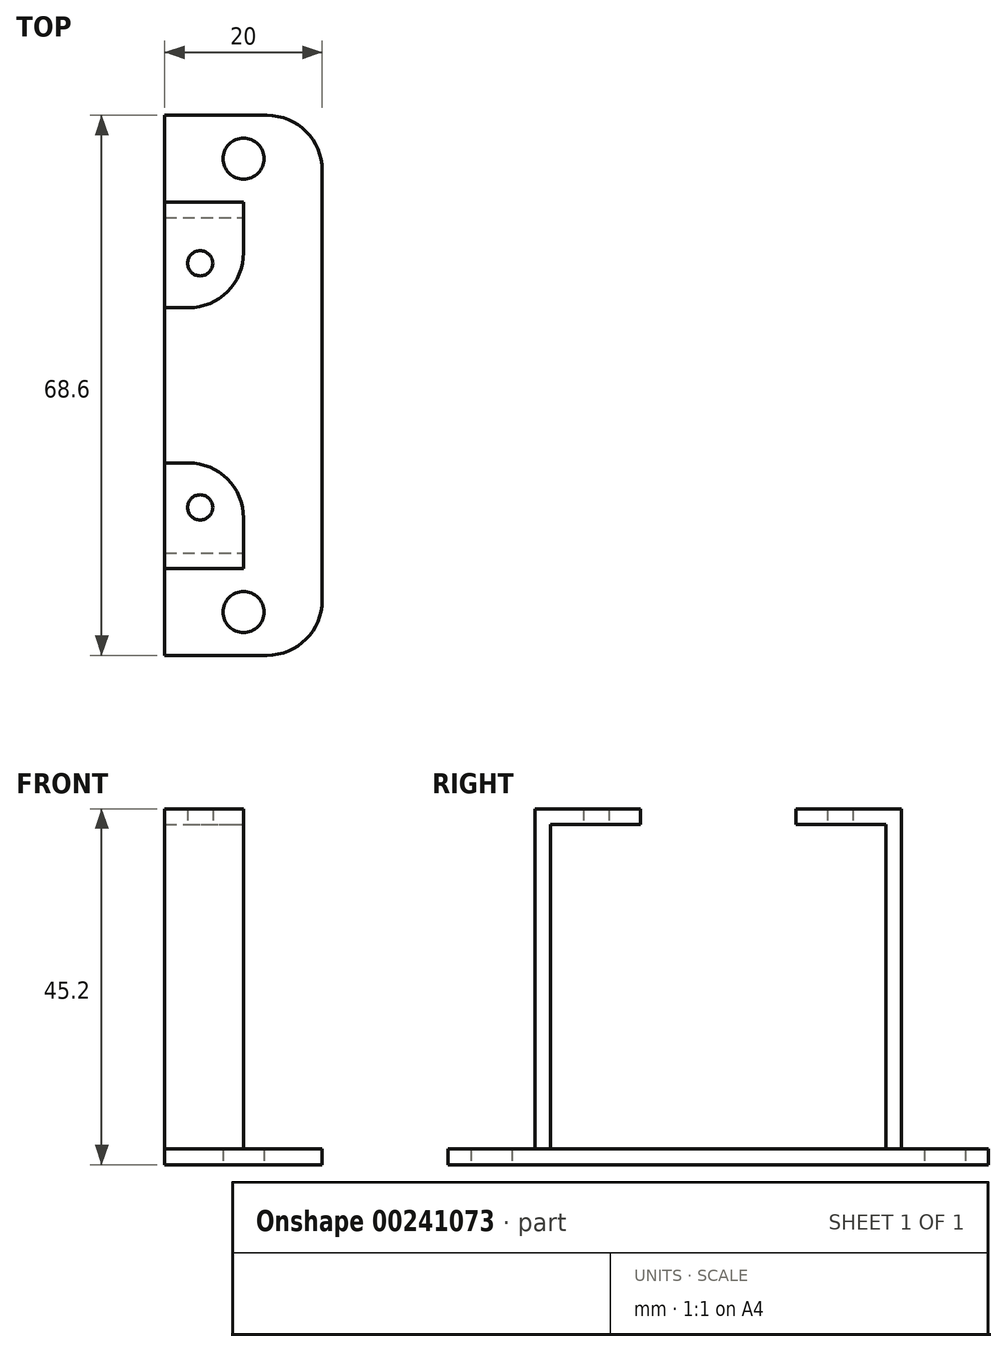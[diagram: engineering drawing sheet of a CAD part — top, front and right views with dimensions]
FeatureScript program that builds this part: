
annotation { "Feature Type Name" : "Feature", "Feature Type Description" : "" }
export const myFeature = defineFeature(function(context is Context, id is Id, definition is map)
    precondition{}
    {
        {
            var Q0;
            Q0=qCreatedBy(makeId("Top.planeOp"),FACE);
            var sketch = newSketch(context, id + "F0", { "sketchPlane" : qUnion([Q0])});
            skLineSegment(sketch, "E0", {"start": v(-61.56, 1.08) * mm, "end": v(-30.56, 1.08) * mm, "construction": true});
            skLineSegment(sketch, "E1", {"start": v(-30.56, 1.08) * mm, "end": v(-30.56, -29.92) * mm, "construction": true});
            skLineSegment(sketch, "E2", {"start": v(-30.56, -29.92) * mm, "end": v(-61.56, -29.92) * mm, "construction": true});
            skLineSegment(sketch, "E3", {"start": v(-61.56, -29.92) * mm, "end": v(-61.56, 1.08) * mm, "construction": true});
            skLineSegment(sketch, "E4", {"start": v(-36.06, 55.81) * mm, "end": v(-36.06, -69.61) * mm, "construction": true});
            skLineSegment(sketch, "E5", {"start": v(-16.06, 55.81) * mm, "end": v(-16.06, -69.61) * mm, "construction": true});
            skLineSegment(sketch, "E6", {"start": v(-6.06, 55.81) * mm, "end": v(-6.06, -69.61) * mm, "construction": true});
            skLineSegment(sketch, "E7.MirrorCS", {"start": v(-56.06, 55.81) * mm, "end": v(-56.06, -69.61) * mm, "construction": true});
            skLineSegment(sketch, "E8.MirrorCS", {"start": v(-66.06, 55.81) * mm, "end": v(-66.06, -69.61) * mm, "construction": true});
            skLineSegment(sketch, "E9.bottom", {"start": v(-67.36, 6.88) * mm, "end": v(-24.76, 6.88) * mm, "construction": true});
            skLineSegment(sketch, "E9.top", {"start": v(-67.36, -35.72) * mm, "end": v(-24.76, -35.72) * mm, "construction": true});
            skLineSegment(sketch, "E9.left", {"start": v(-67.36, 6.88) * mm, "end": v(-67.36, -35.72) * mm, "construction": true});
            skLineSegment(sketch, "E9.right", {"start": v(-24.76, 6.88) * mm, "end": v(-24.76, -35.72) * mm, "construction": true});
            skPoint(sketch, "E10", {"position": v(-24.76, -14.42) * mm});
            skPoint(sketch, "E11", {"position": v(-30.56, -14.42) * mm});
            skPoint(sketch, "E12", {"position": v(-46.06, 1.08) * mm});
            skPoint(sketch, "E13", {"position": v(-46.06, 6.88) * mm});
            skLineSegment(sketch, "E14", {"start": v(-56.06, 55.81) * mm, "end": v(-36.06, 55.81) * mm, "construction": true});
            skPoint(sketch, "E15", {"position": v(-46.06, 55.81) * mm});
            skLineSegment(sketch, "E16", {"start": v(-61.06, 8.88) * mm, "end": v(-61.06, 19.88) * mm, "construction": true});
            skLineSegment(sketch, "E17", {"start": v(-61.06, 19.88) * mm, "end": v(-51.06, 19.88) * mm});
            skLineSegment(sketch, "E18", {"start": v(-51.06, 19.88) * mm, "end": v(-51.06, 8.88) * mm});
            skPoint(sketch, "E19", {"position": v(-56.06, 19.88) * mm});
            skLineSegment(sketch, "E20.bottom", {"start": v(-66.06, 6.88) * mm, "end": v(-56.06, 6.88) * mm});
            skLineSegment(sketch, "E20.top", {"start": v(-66.06, 8.88) * mm, "end": v(-51.06, 8.88) * mm});
            skLineSegment(sketch, "E20.left", {"start": v(-66.06, 6.88) * mm, "end": v(-66.06, 8.88) * mm});
            skLineSegment(sketch, "E21", {"start": v(-95.64, -14.42) * mm, "end": v(16.88, -14.42) * mm, "construction": true});
            skLineSegment(sketch, "E22.MirrorCS", {"start": v(-66.06, -35.72) * mm, "end": v(-51.06, -35.72) * mm});
            skLineSegment(sketch, "E23", {"start": v(-66.06, 6.88) * mm, "end": v(-66.06, -35.72) * mm});
            skLineSegment(sketch, "E24", {"start": v(-56.06, 6.88) * mm, "end": v(-56.06, -35.72) * mm});
            skLineSegment(sketch, "E25", {"start": v(-56.06, 6.88) * mm, "end": v(-56.06, 8.88) * mm});
            skPoint(sketch, "E26.orphan", {"position": v(-51.06, 6.88) * mm});
            skLineSegment(sketch, "E27", {"start": v(-66.06, 8.88) * mm, "end": v(-66.06, 19.88) * mm});
            skLineSegment(sketch, "E28", {"start": v(-66.06, 19.88) * mm, "end": v(-61.06, 19.88) * mm});
            skPoint(sketch, "E29", {"position": v(-56.06, 14.38) * mm});
            skPoint(sketch, "E29.positionSnap0", {"position": v(-51.06, 14.38) * mm});
            skPoint(sketch, "E30", {"position": v(-46.06, -14.42) * mm});
            skLineSegment(sketch, "E31.MirrorCS", {"start": v(-61.06, -48.72) * mm, "end": v(-51.06, -48.72) * mm});
            skLineSegment(sketch, "E32.MirrorCS", {"start": v(-66.06, -48.72) * mm, "end": v(-61.06, -48.72) * mm});
            skLineSegment(sketch, "E33.MirrorCS", {"start": v(-66.06, -37.72) * mm, "end": v(-66.06, -48.72) * mm});
            skLineSegment(sketch, "E34.MirrorCS", {"start": v(-51.06, -48.72) * mm, "end": v(-51.06, -37.72) * mm});
            skLineSegment(sketch, "E35.MirrorCS", {"start": v(-66.06, -37.72) * mm, "end": v(-51.06, -37.72) * mm});
            skLineSegment(sketch, "E36.MirrorCS", {"start": v(-56.06, -35.72) * mm, "end": v(-56.06, -37.72) * mm});
            skLineSegment(sketch, "E37.MirrorCS", {"start": v(-66.06, -35.72) * mm, "end": v(-66.06, -37.72) * mm});
            skPoint(sketch, "E38.MirrorP", {"position": v(-56.06, -43.22) * mm});
            skLineSegment(sketch, "E39", {"start": v(-51.06, 19.88) * mm, "end": v(-46.06, 19.88) * mm});
            skLineSegment(sketch, "E40", {"start": v(-51.06, -48.72) * mm, "end": v(-46.06, -48.72) * mm});
            skPoint(sketch, "E40.endSnap0", {"position": v(-46.06, -35.72) * mm});
            skLineSegment(sketch, "E41", {"start": v(-46.06, 19.88) * mm, "end": v(-46.06, -48.72) * mm});
            skSolve(sketch);
        }
        {
            var Q0;
            Q0=makeQuery(id+"F0.imprint","IMPRINT",FACE,{"disambiguationData":[TD([[makeQuery(id+"F0.imprint","IMPRINT",EDGE,{"derivedFrom":sQuery(id+"F0.wireOp",EDGE,"E20.bottom")}),-1.0]])]});
            var Q1;
            Q1=makeQuery(id+"F0.imprint","IMPRINT",FACE,{"disambiguationData":[TD([[makeQuery(id+"F0.imprint","IMPRINT",EDGE,{"derivedFrom":sQuery(id+"F0.wireOp",EDGE,"E31.MirrorCS")}),1.0]])]});
            var Q2;
            Q2=makeQuery(id+"F0.imprint","IMPRINT",FACE,{"disambiguationData":[TD([[makeQuery(id+"F0.imprint","IMPRINT",EDGE,{"derivedFrom":sQuery(id+"F0.wireOp",EDGE,"E17")}),-1.0]])]});
            var Q3;
            {var subQ1=sQuery(id+"F0.wireOp",EDGE,"E18");Q3=makeQuery(id+"F0.imprint","IMPRINT",FACE,{"disambiguationData":[TD([[makeQuery(id+"F0.imprint","IMPRINT",EDGE,{"derivedFrom":subQ1}),1.0]])]});}
            extrude(context, id + "F1", {"entities" : qUnion([Q0, Q1, Q2, Q3]), "depth" : 2 * mm});
        }
        {
            var Q0;
            {var subQ2=sQuery(id+"F0.wireOp",EDGE,"E36.MirrorCS");Q0=makeQuery(id+"F0.imprint","IMPRINT",FACE,{"disambiguationData":[TD([[makeQuery(id+"F0.imprint","IMPRINT",EDGE,{"derivedFrom":subQ2}),-1.0]])]});}
            var Q1;
            Q1=makeQuery(id+"F0.imprint","IMPRINT",FACE,{"disambiguationData":[TD([[makeQuery(id+"F0.imprint","IMPRINT",EDGE,{"derivedFrom":sQuery(id+"F0.wireOp",EDGE,"E20.bottom")}),1.0]])]});
            extrude(context, id + "F2", {"entities" : qUnion([Q0, Q1]), "operationType" : NewBodyOperationType.ADD, "depth" : 43.2 * mm});
        }
        {
            var Q0;
            Q0=makeQuery(id+"F2.opExtrude","CAP_FACE",FACE,{"disambiguationData":[OSD([sQuery(id+"F0.wireOp",EDGE,"E22.MirrorCS"),sQuery(id+"F0.wireOp",EDGE,"E35.MirrorCS"),sQuery(id+"F0.wireOp",EDGE,"E36.MirrorCS"),sQuery(id+"F0.wireOp",EDGE,"E37.MirrorCS")])],"isStart":false});
            var sketch = newSketch(context, id + "F3", { "sketchPlane" : qUnion([Q0])});
            skLineSegment(sketch, "E42.0.2", {"start": v(-56.06, 8.88) * mm, "end": v(-66.06, 8.88) * mm, "construction": true});
            skLineSegment(sketch, "E43.0", {"start": v(-95.64, -14.42) * mm, "end": v(16.88, -14.42) * mm, "construction": true});
            skLineSegment(sketch, "E44.MirrorCS", {"start": v(-56.06, -37.72) * mm, "end": v(-66.06, -37.72) * mm, "construction": true});
            skLineSegment(sketch, "E45.bottom", {"start": v(-66.06, 8.88) * mm, "end": v(-56.06, 8.88) * mm});
            skLineSegment(sketch, "E45.top", {"start": v(-66.06, -37.72) * mm, "end": v(-56.06, -37.72) * mm});
            skLineSegment(sketch, "E45.left", {"start": v(-66.06, 8.88) * mm, "end": v(-66.06, -4.57) * mm});
            skLineSegment(sketch, "E45.right", {"start": v(-56.06, 8.88) * mm, "end": v(-56.06, -4.57) * mm});
            skLineSegment(sketch, "E46.0", {"start": v(-30.56, -29.92) * mm, "end": v(-61.56, -29.92) * mm, "construction": true});
            skLineSegment(sketch, "E47.0", {"start": v(-61.56, 1.08) * mm, "end": v(-30.56, 1.08) * mm, "construction": true});
            skPoint(sketch, "E48", {"position": v(-61.56, 1.08) * mm});
            skPoint(sketch, "E49", {"position": v(-61.56, -29.92) * mm});
            skLineSegment(sketch, "E50", {"start": v(-66.06, -4.57) * mm, "end": v(-56.06, -4.57) * mm});
            skLineSegment(sketch, "E51.MirrorCS", {"start": v(-66.06, -24.27) * mm, "end": v(-56.06, -24.27) * mm});
            skLineSegment(sketch, "E52.trimOffspring", {"start": v(-66.06, -24.27) * mm, "end": v(-66.06, -37.72) * mm});
            skLineSegment(sketch, "E53.trimOffspring", {"start": v(-56.06, -24.27) * mm, "end": v(-56.06, -37.72) * mm});
            skSolve(sketch);
        }
        {
            var Q0;
            {var subQ0=sQuery(id+"F3.wireOp",EDGE,"E45.top");Q0=makeQuery(id+"F3.imprint","IMPRINT",FACE,{"disambiguationData":[TD([[makeQuery(id+"F3.imprint","IMPRINT",EDGE,{"derivedFrom":subQ0}),1.0]])]});}
            var Q1;
            {var subQ0=sQuery(id+"F3.wireOp",EDGE,"E45.bottom");Q1=makeQuery(id+"F3.imprint","IMPRINT",FACE,{"disambiguationData":[TD([[makeQuery(id+"F3.imprint","IMPRINT",EDGE,{"derivedFrom":subQ0}),-1.0]])]});}
            var Q2;
            {var subQ0=sQuery(id+"F3.wireOp",EDGE,"E51.MirrorCS");Q2=makeQuery(id+"F3.imprint","IMPRINT",FACE,{"disambiguationData":[TD([[makeQuery(id+"F3.imprint","IMPRINT",EDGE,{"derivedFrom":subQ0}),-1.0]])]});}
            extrude(context, id + "F4", {"entities" : qUnion([Q0, Q1, Q2]), "operationType" : NewBodyOperationType.ADD, "depth" : 2 * mm});
        }
        {
            var Q0;
            Q0=sQuery(id+"F3.wireOp",VERTEX,"E48");
            var Q1;
            Q1=sQuery(id+"F3.wireOp",VERTEX,"E49");
            var Q2;
            Q2=makeQuery(id+"F1.opExtrude","SWEPT_BODY",BODY,{"disambiguationData":[OSD([sQuery(id+"F0.wireOp",EDGE,"E17"),sQuery(id+"F0.wireOp",EDGE,"E18"),sQuery(id+"F0.wireOp",EDGE,"E20.top"),sQuery(id+"F0.wireOp",EDGE,"E27"),sQuery(id+"F0.wireOp",EDGE,"E28")])]});
            hole(context, id + "F5", {"style" : HoleStyle.SIMPLE, "endStyle" : HoleEndStyle.THROUGH, "oppositeDirection" : true, "holeDiameter" : 3.2 * mm, "locations" : qUnion([Q0, Q1]), "scope" : qUnion([Q2]), "isTappedThrough" : true});
        }
        {
            var Q0;
            Q0=sQuery(id+"F0.wireOp",VERTEX,"E29");
            var Q1;
            Q1=sQuery(id+"F0.wireOp",VERTEX,"E38.MirrorP");
            var Q2;
            Q2=makeQuery(id+"F1.opExtrude","SWEPT_BODY",BODY,{"disambiguationData":[OSD([sQuery(id+"F0.wireOp",EDGE,"E17"),sQuery(id+"F0.wireOp",EDGE,"E18"),sQuery(id+"F0.wireOp",EDGE,"E20.top"),sQuery(id+"F0.wireOp",EDGE,"E27"),sQuery(id+"F0.wireOp",EDGE,"E28")])]});
            hole(context, id + "F6", {"style" : HoleStyle.SIMPLE, "endStyle" : HoleEndStyle.THROUGH, "oppositeDirection" : true, "holeDiameter" : 5.2 * mm, "locations" : qUnion([Q0, Q1]), "scope" : qUnion([Q2]), "isTappedThrough" : true});
        }
        {
            var Q0;
            Q0=makeQuery(id+"F4.opExtrude","SWEPT_EDGE",EDGE,{"disambiguationData":[OSD([sQuery(id+"F3.wireOp",EDGE,"E45.right"),sQuery(id+"F3.wireOp",EDGE,"E50")])]});
            var Q1;
            Q1=makeQuery(id+"F4.opExtrude","SWEPT_EDGE",EDGE,{"disambiguationData":[OSD([sQuery(id+"F3.wireOp",EDGE,"E51.MirrorCS"),sQuery(id+"F3.wireOp",EDGE,"E53.trimOffspring")])]});
            var Q2;
            Q2=makeQuery(id+"F1.opExtrude","SWEPT_EDGE",EDGE,{"disambiguationData":[OSD([sQuery(id+"F0.wireOp",EDGE,"E39"),sQuery(id+"F0.wireOp",EDGE,"E41")])]});
            var Q3;
            Q3=makeQuery(id+"F1.opExtrude","SWEPT_EDGE",EDGE,{"disambiguationData":[OSD([sQuery(id+"F0.wireOp",EDGE,"E40"),sQuery(id+"F0.wireOp",EDGE,"E41")])]});
            fillet(context, id + "F7", {"entities" : qUnion([Q0, Q1, Q2, Q3]), "radius" : 7 * mm, "tangentPropagation" : true, "allowEdgeOverflow" : false});
        }
    });
